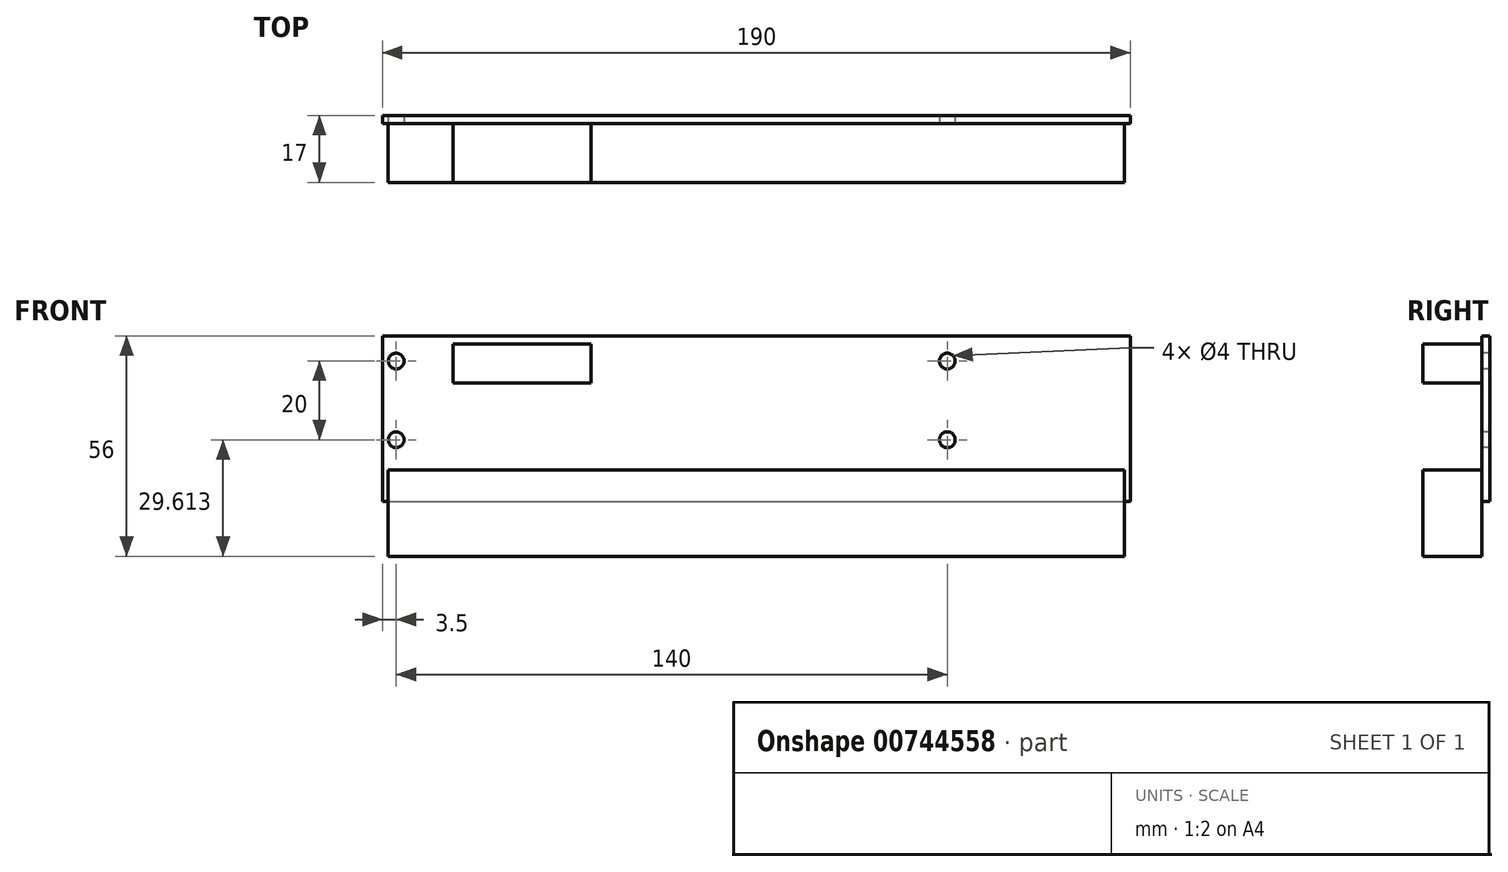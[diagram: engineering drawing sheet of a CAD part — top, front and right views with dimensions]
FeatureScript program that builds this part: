
annotation { "Feature Type Name" : "Feature", "Feature Type Description" : "" }
export const myFeature = defineFeature(function(context is Context, id is Id, definition is map)
    precondition{}
    {
        {
            var Q0;
            Q0=qCreatedBy(makeId("Front.planeOp"),FACE);
            var sketch = newSketch(context, id + "F0", { "sketchPlane" : qUnion([Q0])});
            skLineSegment(sketch, "E0.bottom", {"start": v(-95, 21) * mm, "end": v(95, 21) * mm});
            skLineSegment(sketch, "E0.top", {"start": v(-95, -21) * mm, "end": v(95, -21) * mm});
            skLineSegment(sketch, "E0.left", {"start": v(-95, 21) * mm, "end": v(-95, -21) * mm});
            skLineSegment(sketch, "E0.right", {"start": v(95, 21) * mm, "end": v(95, -21) * mm});
            skSolve(sketch);
        }
        {
            var Q0;
            Q0 = qSketchRegion(id + "F0", true);
            extrude(context, id + "F1", {"entities" : qUnion([Q0]), "depth" : 2 * mm, "offsetDistance" : 25 * mm});
        }
        {
            var Q0;
            Q0=makeQuery(id+"F1.opExtrude","CAP_FACE",FACE,{"disambiguationData":[OSD([sQuery(id+"F0.wireOp",EDGE,"E0.bottom"),sQuery(id+"F0.wireOp",EDGE,"E0.top"),sQuery(id+"F0.wireOp",EDGE,"E0.left"),sQuery(id+"F0.wireOp",EDGE,"E0.right")])],"isStart":false});
            var sketch = newSketch(context, id + "F2", { "sketchPlane" : qUnion([Q0])});
            skCircle(sketch, "E1", {"center": v(48.5, 14.61) * mm, "radius": 2 * mm});
            skCircle(sketch, "E2.0.1.0", {"center": v(48.5, -5.39) * mm, "radius": 2 * mm});
            skCircle(sketch, "E2.1.0.0", {"center": v(-91.5, 14.61) * mm, "radius": 2 * mm});
            skCircle(sketch, "E2.1.1.0", {"center": v(-91.5, -5.39) * mm, "radius": 2 * mm});
            skLineSegment(sketch, "E2.direction1", {"start": v(48.5, 14.61) * mm, "end": v(-91.5, 14.61) * mm, "construction": true});
            skLineSegment(sketch, "E2.direction2", {"start": v(48.5, 14.61) * mm, "end": v(48.5, -5.39) * mm, "construction": true});
            skSolve(sketch);
        }
        {
            var Q0;
            Q0=sQuery(id+"F2.wireOp",VERTEX,"E2.direction1.end");
            var Q1;
            Q1=sQuery(id+"F2.wireOp",VERTEX,"E2.1.1.0.center");
            var Q2;
            Q2=sQuery(id+"F2.wireOp",VERTEX,"E2.direction1.start");
            var Q3;
            Q3=sQuery(id+"F2.wireOp",VERTEX,"E2.direction2.end");
            var Q4;
            Q4=makeQuery(id+"F1.opExtrude","SWEPT_BODY",BODY,{"disambiguationData":[OSD([sQuery(id+"F0.wireOp",EDGE,"E0.bottom"),sQuery(id+"F0.wireOp",EDGE,"E0.top"),sQuery(id+"F0.wireOp",EDGE,"E0.left"),sQuery(id+"F0.wireOp",EDGE,"E0.right")])]});
            hole(context, id + "F3", {"style" : HoleStyle.SIMPLE, "endStyle" : HoleEndStyle.THROUGH, "standardTappedOrClearance" : lookupTablePath({ "standard" : "ISO", "size" : "4", "type" : "Drilled" }), "standardBlindInLast" : lookupTablePath({ "standard" : "ISO", "size" : "4", "type" : "Drilled" }), "holeDiameter" : 4 * mm, "majorDiameter" : 5 * mm, "isTappedThrough" : true, "tappedDepth" : 12 * mm, "tapClearance" : 3, "locations" : qUnion([Q0, Q1, Q2, Q3]), "scope" : qUnion([Q4])});
        }
        {
            var Q0;
            Q0=makeQuery(id+"F1.opExtrude","CAP_FACE",FACE,{"disambiguationData":[OSD([sQuery(id+"F0.wireOp",EDGE,"E0.bottom"),sQuery(id+"F0.wireOp",EDGE,"E0.top"),sQuery(id+"F0.wireOp",EDGE,"E0.left"),sQuery(id+"F0.wireOp",EDGE,"E0.right")])],"isStart":false});
            var sketch = newSketch(context, id + "F4", { "sketchPlane" : qUnion([Q0])});
            skLineSegment(sketch, "E3.bottom", {"start": v(-77, 19) * mm, "end": v(-42, 19) * mm});
            skLineSegment(sketch, "E3.top", {"start": v(-77, 9) * mm, "end": v(-42, 9) * mm});
            skLineSegment(sketch, "E3.left", {"start": v(-77, 19) * mm, "end": v(-77, 9) * mm});
            skLineSegment(sketch, "E3.right", {"start": v(-42, 19) * mm, "end": v(-42, 9) * mm});
            skLineSegment(sketch, "E4.bottom", {"start": v(-93.5, -13) * mm, "end": v(93.5, -13) * mm});
            skLineSegment(sketch, "E4.top", {"start": v(-93.5, -35) * mm, "end": v(93.5, -35) * mm});
            skLineSegment(sketch, "E4.left", {"start": v(-93.5, -13) * mm, "end": v(-93.5, -35) * mm});
            skLineSegment(sketch, "E4.right", {"start": v(93.5, -13) * mm, "end": v(93.5, -35) * mm});
            skSolve(sketch);
        }
        {
            var Q0;
            Q0 = qSketchRegion(id + "F4", true);
            extrude(context, id + "F5", {"entities" : qUnion([Q0]), "operationType" : NewBodyOperationType.ADD, "depth" : 15 * mm, "offsetDistance" : 25 * mm});
        }
    });
